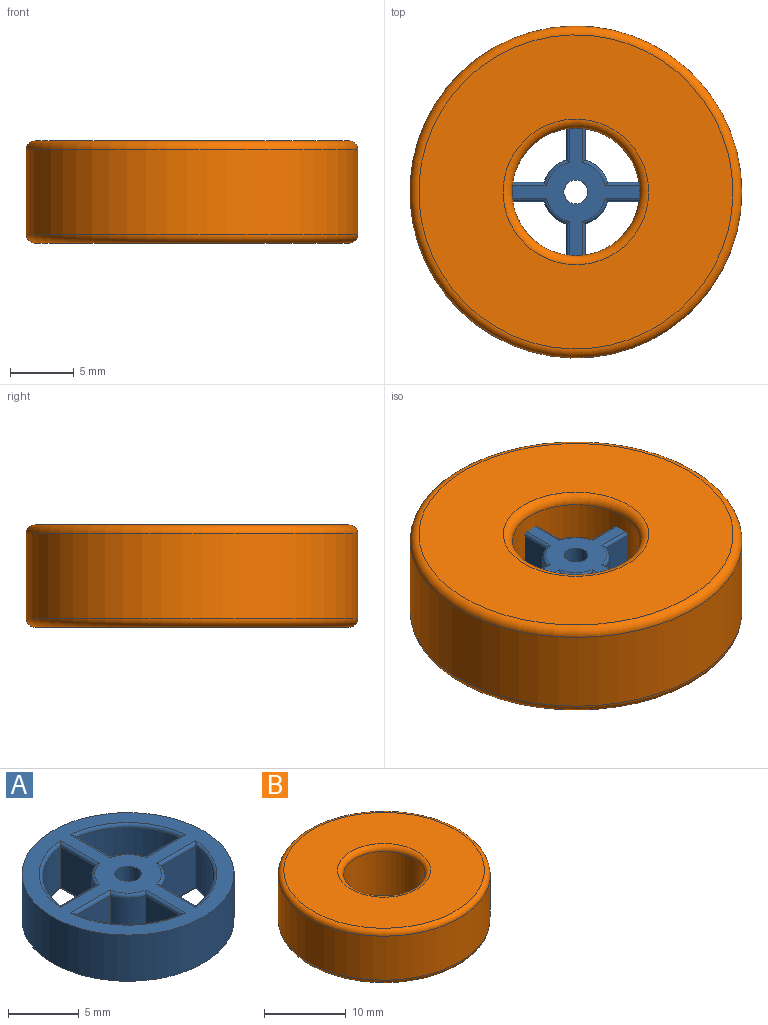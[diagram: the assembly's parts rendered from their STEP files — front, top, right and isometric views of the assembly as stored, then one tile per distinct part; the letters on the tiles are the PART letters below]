
ASSEMBLY  parts=2 mates=1
PART A: 50 faces, bbox 15x15x4 mm
  f0: cylinder r=2.61mm len=3.5mm, axis (0,0,-1), area 9mm2, adj f1,f17,f20,f34
  f1: plane 3.5x3.5mm, normal (0,1,0), area 12.2mm2, adj f0,f2,f21,f35
  f2: cylinder r=6.1mm len=5.25mm, axis (0,0,-1), area 27.9mm2, adj f1,f17,f23,f37
  f3: cylinder r=6.1mm len=5.25mm, axis (0,0,-1), area 27.9mm2, adj f4,f14,f26,f40
  f4: plane 3.5x3.5mm, normal (0,1,0), area 12.2mm2, adj f3,f5,f24,f38
  f5: cylinder r=2.61mm len=3.5mm, axis (0,0,-1), area 9mm2, adj f4,f14,f25,f39
  f6: cylinder r=2.61mm len=3.5mm, axis (0,0,-1), area 9mm2, adj f7,f15,f29,f43
  f7: plane 3.5x3.5mm, normal (0,-1,0), area 12.2mm2, adj f6,f8,f28,f42
  f8: cylinder r=6.1mm len=5.25mm, axis (0,0,-1), area 27.9mm2, adj f7,f15,f30,f44
  f9: cylinder r=6.1mm len=5.25mm, axis (0,0,-1), area 27.9mm2, adj f10,f16,f33,f48
  f10: plane 4.03x3.76mm, normal (0,-1,0), area 13.2mm2, adj f9,f11,f19,f32,f33,f46
  f11: cylinder r=2.61mm len=3.5mm, axis (0,0,-1), area 9mm2, adj f10,f16,f32,f47
  f12: cylinder r=7.5mm len=15mm, axis (0,0,-1), area 188.5mm2, adj f18,f19
  f13: cylinder r=0.93mm len=4mm, axis (0,0,-1), area 23.4mm2, adj f18,f19
  f14: plane 3.5x3.5mm, normal (1,0,0), area 12.2mm2, adj f3,f5,f27,f41
  f15: plane 3.5x3.5mm, normal (1,0,0), area 12.2mm2, adj f6,f8,f31,f45
  f16: plane 4.03x3.76mm, normal (-1,0,0), area 13.2mm2, adj f9,f11,f19,f32,f33,f49
  f17: plane 3.5x3.5mm, normal (-1,0,0), area 12.2mm2, adj f0,f2,f22,f36
  f18: plane 15x15mm, normal (0,0,1), area 83mm2, adj f12,f13,f34,f35,f36,f37,f38,f39
  f19: plane 15x15mm, normal (0,0,-1), area 85mm2, adj f10,f12,f13,f16,f20,f21,f22,f23
  f20: torus R=2.36mm, axis (0,0,1), area 1mm2, adj f0,f19,f21,f22
  f21: cylinder r=0.25mm len=3.97mm, axis (-1,0,0), area 1.4mm2, adj f1,f19,f20,f23
  f22: cylinder r=0.25mm len=3.97mm, axis (0,-1,0), area 1.4mm2, adj f17,f19,f20,f23
  f23: torus R=6.35mm, axis (0,0,1), area 3.3mm2, adj f2,f19,f21,f22
  f24: cylinder r=0.25mm len=3.97mm, axis (-1,0,0), area 1.4mm2, adj f4,f19,f25,f26
  f25: torus R=2.36mm, axis (0,0,1), area 1mm2, adj f5,f19,f24,f27
  f26: torus R=6.35mm, axis (0,0,1), area 3.3mm2, adj f3,f19,f24,f27
  f27: cylinder r=0.25mm len=3.97mm, axis (0,1,0), area 1.4mm2, adj f14,f19,f25,f26
  f28: cylinder r=0.25mm len=3.97mm, axis (1,0,0), area 1.4mm2, adj f7,f19,f29,f30
  f29: torus R=2.36mm, axis (0,0,1), area 1mm2, adj f6,f19,f28,f31
  f30: torus R=6.35mm, axis (0,0,1), area 3.3mm2, adj f8,f19,f28,f31
  f31: cylinder r=0.25mm len=3.97mm, axis (0,1,0), area 1.4mm2, adj f15,f19,f29,f30
  f32: torus R=2.36mm, axis (0,0,1), area 1mm2, adj f10,f11,f16,f19
  f33: torus R=6.35mm, axis (0,0,1), area 3.2mm2, adj f9,f10,f16,f19
  f34: torus R=2.36mm, axis (0,0,1), area 1mm2, adj f0,f18,f35,f36
  f35: cylinder r=0.25mm len=3.97mm, axis (1,0,0), area 1.4mm2, adj f1,f18,f34,f37
  f36: cylinder r=0.25mm len=3.97mm, axis (0,1,0), area 1.4mm2, adj f17,f18,f34,f37
  f37: torus R=6.35mm, axis (0,0,1), area 3.3mm2, adj f2,f18,f35,f36
  f38: cylinder r=0.25mm len=3.97mm, axis (1,0,0), area 1.4mm2, adj f4,f18,f39,f40
  f39: torus R=2.36mm, axis (0,0,1), area 1mm2, adj f5,f18,f38,f41
  f40: torus R=6.35mm, axis (0,0,1), area 3.3mm2, adj f3,f18,f38,f41
  f41: cylinder r=0.25mm len=3.97mm, axis (0,-1,0), area 1.4mm2, adj f14,f18,f39,f40
  f42: cylinder r=0.25mm len=3.97mm, axis (-1,0,0), area 1.4mm2, adj f7,f18,f43,f44
  f43: torus R=2.36mm, axis (0,0,1), area 1mm2, adj f6,f18,f42,f45
  f44: torus R=6.35mm, axis (0,0,1), area 3.3mm2, adj f8,f18,f42,f45
  f45: cylinder r=0.25mm len=3.97mm, axis (0,-1,0), area 1.4mm2, adj f15,f18,f43,f44
  f46: cylinder r=0.25mm len=3.97mm, axis (-1,0,0), area 1.4mm2, adj f10,f18,f47,f48
  f47: torus R=2.36mm, axis (0,0,1), area 1mm2, adj f11,f18,f46,f49
  f48: torus R=6.35mm, axis (0,0,1), area 3.3mm2, adj f9,f18,f46,f49
  f49: cylinder r=0.25mm len=3.97mm, axis (0,1,0), area 1.4mm2, adj f16,f18,f47,f48
PART B: 8 faces, bbox 28.1x28.1x8 mm
  f0: cylinder r=5mm len=10mm, axis (0,0,-1), area 207.3mm2, adj f4,f6
  f1: cylinder r=13mm len=26mm, axis (0,0,-1), area 539.1mm2, adj f5,f7
  f2: plane 24.6x24.6mm, normal (0,0,1), area 373.2mm2, adj f6,f7
  f3: plane 24.6x24.6mm, normal (0,0,-1), area 373.2mm2, adj f4,f5
  f4: torus R=5.7mm, axis (0,0,1), area 36.3mm2, adj f0,f3
  f5: torus R=12.3mm, axis (0,0,1), area 88.1mm2, adj f1,f3
  f6: torus R=5.7mm, axis (0,0,1), area 36.3mm2, adj f0,f2
  f7: torus R=12.3mm, axis (0,0,1), area 88.1mm2, adj f1,f2
PLACE A t=(-1.82,-2.08,-0.57)mm
PLACE B t=(-1.82,-2.08,-4.57)mm
MATE cylindrical B.f0 <-> A.f12  axis (0,0,1) through (-1.82,-2.08,1.43)mm
